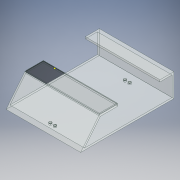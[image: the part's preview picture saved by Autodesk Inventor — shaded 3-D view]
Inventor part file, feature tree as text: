
AUTODESK INVENTOR PART (.ipt)
format: ipt  version: 2018 (Build 220112000, 112)  size: 187,392 bytes
history: native  units: in
note: dims shown in document units (in); Inventor stores cm internally (conversion verified against a paired STEP export)
features: sketch x5, extrude x3, fillet x1
ambient origin geometry x8: Origin, YZ Plane, XZ Plane, XY Plane, X Axis, Y Axis, Z Axis, Center Point
bodies: Solid1 (feature_tree)
feature tree (9):
  sketch  "Sketch1"  dims[d3=7.874in d4=1.5748in]
  extrude  "Extrusion1"  Depth=1.5748in
  extrude  "Extrusion2"  Depth=1.1811in
  sketch  "Sketch5"  dims[d12=0.1575in]
  extrude  "Extrusion4"  Depth=0.1575in
  fillet  "Fillet1"  Radius=0.1575in
  sketch  "Sketch2"  dims[d5=1.9685in d6=1.1811in]
  sketch  "Sketch3"  dims[d7=1.5748in d9=0.3528in d10=0.1575in]
  sketch  "Sketch6"  dims[d14=0.1575in d15=0.1575in d16=0.1575in d17=0.1575in d18=0.1575in d19=6.2992in d20=0.0in d21=0.0394in d22=0.0394in d23=0.0394in d24=0.0394in d25=0.0787in d26=0.0in d33=0.1969in d34=0.2362in d35=0.7874in d36=2.9528in d37=0.1969in d38=0.2362in d39=0.1969in d40=0.2362in d41=0.1969in d42=0.2362in d43=2.9528in d44=0.7874in d45=0.7874in d46=0.7874in d47=2.9528in d48=2.9528in d49=0.1181in d50=0.0in d51=0.0787in]
